# Revit family: equip-water-cooler-elkay-efrpcm8
name_source: partatom
category: Plumbing Fixtures
units: mm (PartAtom-declared; Revit-internal decimal feet)

## family parameters
Always vertical = Yes
Cut with Voids When Loaded = No
Host = Wall
OmniClass Number = 23.45.00.00
OmniClass Title = Sanitary, Laundry, and Cleaning Equipment
Part Type = Normal
Room Calculation Point = No
Round Connector Dimension = Use Diameter
Shared = No

## types (1)
- equip-water-cooler-elkay-efrpcm8
    Activation = Mechanical
    Bubbler = FlexiGuard Safety
    CW Connection = Yes
    Chiller = ECP8
    Chiller Option = Yes
    Description = Water Cooler/Cuspidor
    Fountain = EFRPCM8
    HW Connection = No
    Manufacturer = Elkay
    Model = EFRPCM8
    Mounting = Recessed Mount
    Type = Single
    URL = http://www.elkay.com
    Vent Connection = No
    Volts/Hertz = 115V/60Hz
    Waste Connection = Yes

## geometry (parser evidence)
native form markers: Sweep x6
no freeform markers — native parametric forms only
